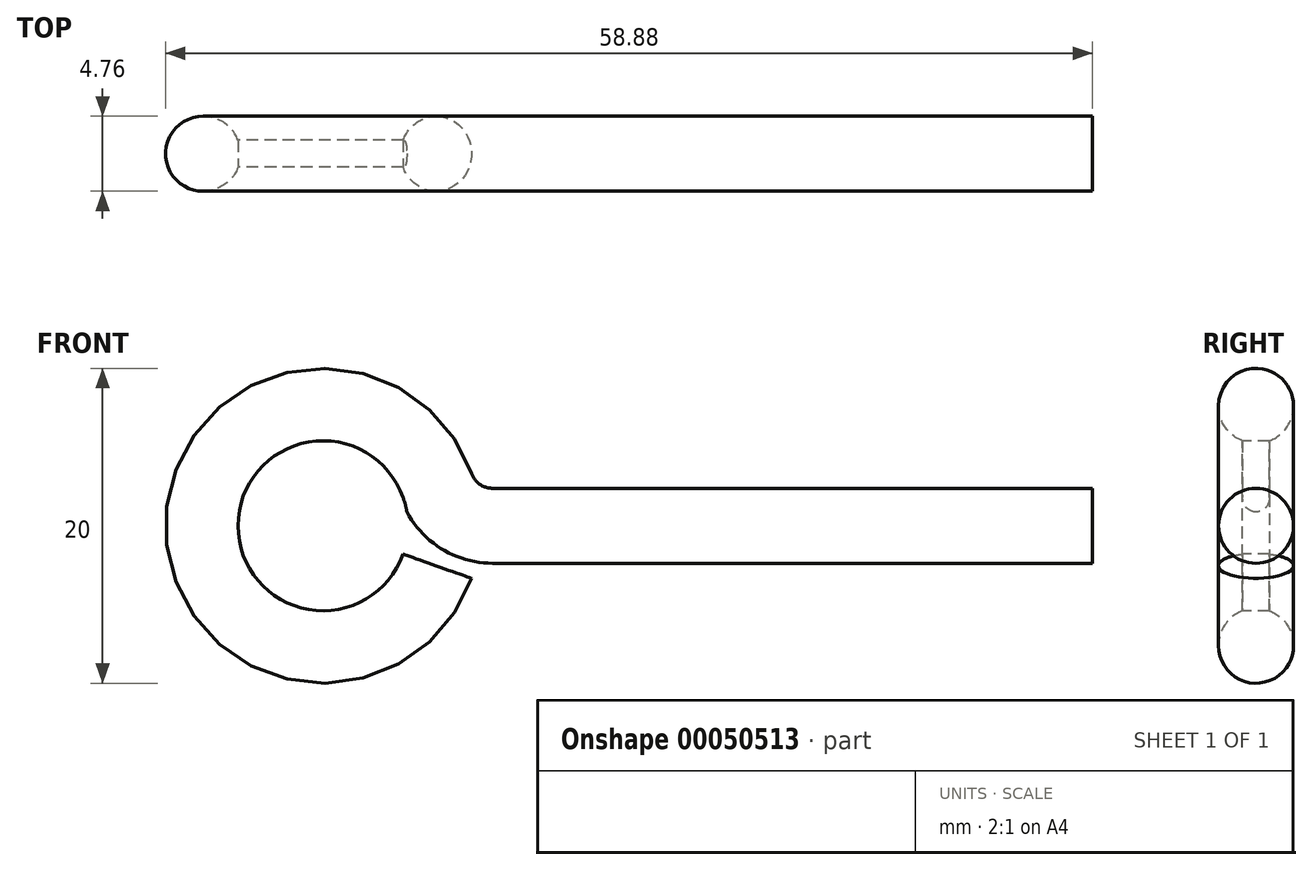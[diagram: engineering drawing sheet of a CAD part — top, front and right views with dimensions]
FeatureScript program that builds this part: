
annotation { "Feature Type Name" : "Feature", "Feature Type Description" : "" }
export const myFeature = defineFeature(function(context is Context, id is Id, definition is map)
    precondition{}
    {
        {
            var Q0;
            Q0=qCreatedBy(makeId("Right.planeOp"),FACE);
            var sketch = newSketch(context, id + "F0", { "sketchPlane" : qUnion([Q0])});
            skCircle(sketch, "E0", {"center": v(0, 0) * mm, "radius": 2.38 * mm});
            skSolve(sketch);
        }
        {
            var Q0;
            Q0=qCreatedBy(makeId("Front.planeOp"),FACE);
            var sketch = newSketch(context, id + "F1", { "sketchPlane" : qUnion([Q0])});
            skLineSegment(sketch, "E1", {"start": v(0, 0) * mm, "end": v(-38.1, 0) * mm});
            skArc(sketch, "E2", {"start": v(-41.7, 2.54) * mm, "mid": v(-40.3, 0.7) * mm, "end": v(-38.1, 0) * mm});
            skArc(sketch, "E3", {"start": v(-41.7, 2.54) * mm, "mid": v(-56.5, 0) * mm, "end": v(-41.7, -2.54) * mm});
            skSolve(sketch);
        }
        {
            var Q0;
            Q0 = qSketchRegion(id + "F0", true);
            var Q1;
            Q1=sQuery(id+"F1.wireOp",EDGE,"E1");
            var Q2;
            Q2=sQuery(id+"F1.wireOp",EDGE,"E2");
            var Q3;
            Q3=sQuery(id+"F1.wireOp",EDGE,"E3");
            sweep(context, id + "F2", {"profiles" : qUnion([Q0]), "path" : qUnion([Q1, Q2, Q3])});
        }
        {
            var Q0;
            Q0=qCreatedBy(makeId("Front.planeOp"),FACE);
            var sketch = newSketch(context, id + "F3", { "sketchPlane" : qUnion([Q0])});
            skCircle(sketch, "E4", {"center": v(-48.88, 0) * mm, "radius": 5.4 * mm});
            skArc(sketch, "E5", {"start": v(-43.94, 1.75) * mm, "mid": v(-54.12, 0) * mm, "end": v(-43.94, -1.75) * mm, "construction": true});
            skSolve(sketch);
        }
        {
            var Q0;
            Q0 = qSketchRegion(id + "F3", true);
            extrude(context, id + "F4", {"entities" : qUnion([Q0]), "operationType" : NewBodyOperationType.REMOVE, "endBound" : BoundingType.SYMMETRIC, "oppositeDirection" : true, "depth" : 25.4 * mm});
        }
    });
